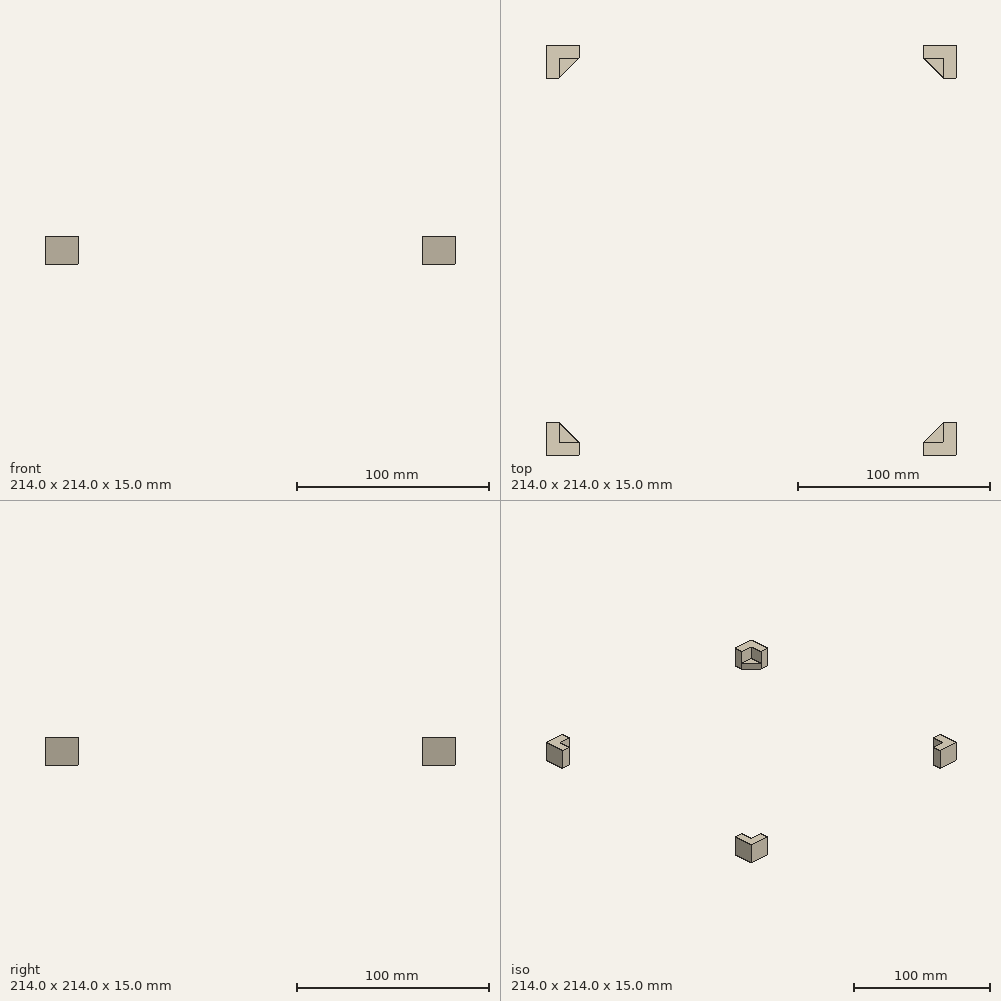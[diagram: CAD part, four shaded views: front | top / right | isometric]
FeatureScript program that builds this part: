
annotation { "Feature Type Name" : "Feature", "Feature Type Description" : "" }
export const myFeature = defineFeature(function(context is Context, id is Id, definition is map)
    precondition{}
    {
        {
            var Q0;
            Q0=qCreatedBy(makeId("Top.planeOp"),FACE);
            var sketch = newSketch(context, id + "F0", { "sketchPlane" : qUnion([Q0])});
            skLineSegment(sketch, "E0.bottom", {"start": v(-107, 107) * mm, "end": v(107, 107) * mm});
            skLineSegment(sketch, "E0.top", {"start": v(-107, -107) * mm, "end": v(107, -107) * mm});
            skLineSegment(sketch, "E0.left", {"start": v(-107, 107) * mm, "end": v(-107, -107) * mm});
            skLineSegment(sketch, "E0.right", {"start": v(107, 107) * mm, "end": v(107, -107) * mm});
            skPoint(sketch, "E0.middle", {"position": v(0, 0) * mm});
            skLineSegment(sketch, "E1.bottom", {"start": v(100, 100) * mm, "end": v(-100, 100) * mm});
            skLineSegment(sketch, "E1.top", {"start": v(100, -100) * mm, "end": v(-100, -100) * mm});
            skLineSegment(sketch, "E1.left", {"start": v(100, 100) * mm, "end": v(100, -100) * mm});
            skLineSegment(sketch, "E1.right", {"start": v(-100, 100) * mm, "end": v(-100, -100) * mm});
            skLineSegment(sketch, "E2.bottom", {"start": v(107, -90) * mm, "end": v(100, -90) * mm});
            skLineSegment(sketch, "E2.top", {"start": v(107, 90) * mm, "end": v(100, 90) * mm});
            skLineSegment(sketch, "E3.left", {"start": v(90, -107) * mm, "end": v(90, -100) * mm});
            skLineSegment(sketch, "E3.right", {"start": v(-90, -107) * mm, "end": v(-90, -100) * mm});
            skLineSegment(sketch, "E4.trimOffspring", {"start": v(-100, 90) * mm, "end": v(-107, 90) * mm});
            skLineSegment(sketch, "E5.trimOffspring", {"start": v(-90, 100) * mm, "end": v(-90, 107) * mm});
            skPoint(sketch, "E6.orphan", {"position": v(-178.54, 90) * mm});
            skPoint(sketch, "E7.orphan", {"position": v(-178.54, -90) * mm});
            skPoint(sketch, "E3.bottom.end.orphan", {"position": v(-90, -205.53) * mm});
            skPoint(sketch, "E8.orphan", {"position": v(90, -205.53) * mm});
            skPoint(sketch, "E3.top.end.orphan", {"position": v(-90, 205.53) * mm});
            skPoint(sketch, "E2.left.start.orphan", {"position": v(178.54, -90) * mm});
            skPoint(sketch, "E9.orphan", {"position": v(178.54, 90) * mm});
            skPoint(sketch, "E10.orphan", {"position": v(90, 205.53) * mm});
            skLineSegment(sketch, "E11.trimOffspring", {"start": v(-100, -90) * mm, "end": v(-107, -90) * mm});
            skLineSegment(sketch, "E12.trimOffspring", {"start": v(90, 100) * mm, "end": v(90, 107) * mm});
            skLineSegment(sketch, "E13", {"start": v(100, -90) * mm, "end": v(90, -100) * mm});
            skLineSegment(sketch, "E14", {"start": v(90, 100) * mm, "end": v(100, 90) * mm});
            skLineSegment(sketch, "E15", {"start": v(-90, -100) * mm, "end": v(-100, -90) * mm});
            skLineSegment(sketch, "E16", {"start": v(-100, 90) * mm, "end": v(-90, 100) * mm});
            skSolve(sketch);
        }
        {
            var Q0;
            {var subQ5=sQuery(id+"F0.wireOp",EDGE,"E4.trimOffspring");Q0=makeQuery(id+"F0.imprint","IMPRINT",FACE,{"disambiguationData":[TD([[makeQuery(id+"F0.imprint","IMPRINT",EDGE,{"derivedFrom":subQ5}),-1.0]])]});}
            var Q1;
            {var subQ4=sQuery(id+"F0.wireOp",EDGE,"E3.right");Q1=makeQuery(id+"F0.imprint","IMPRINT",FACE,{"disambiguationData":[TD([[makeQuery(id+"F0.imprint","IMPRINT",EDGE,{"derivedFrom":subQ4}),1.0]])]});}
            var Q2;
            {var subQ3=sQuery(id+"F0.wireOp",EDGE,"E2.bottom");Q2=makeQuery(id+"F0.imprint","IMPRINT",FACE,{"disambiguationData":[TD([[makeQuery(id+"F0.imprint","IMPRINT",EDGE,{"derivedFrom":subQ3}),1.0]])]});}
            var Q3;
            {var subQ4=sQuery(id+"F0.wireOp",EDGE,"E2.top");Q3=makeQuery(id+"F0.imprint","IMPRINT",FACE,{"disambiguationData":[TD([[makeQuery(id+"F0.imprint","IMPRINT",EDGE,{"derivedFrom":subQ4}),-1.0]])]});}
            extrude(context, id + "F1", {"entities" : qUnion([Q0, Q1, Q2, Q3]), "depth" : 15 * mm, "offsetDistance" : 25 * mm});
        }
        {
            var Q0;
            {var subQ3=sQuery(id+"F0.wireOp",EDGE,"E16");Q0=makeQuery(id+"F0.imprint","IMPRINT",FACE,{"disambiguationData":[TD([[makeQuery(id+"F0.imprint","IMPRINT",EDGE,{"derivedFrom":subQ3}),1.0]])]});}
            var Q1;
            {var subQ3=sQuery(id+"F0.wireOp",EDGE,"E15");Q1=makeQuery(id+"F0.imprint","IMPRINT",FACE,{"disambiguationData":[TD([[makeQuery(id+"F0.imprint","IMPRINT",EDGE,{"derivedFrom":subQ3}),1.0]])]});}
            var Q2;
            {var subQ3=sQuery(id+"F0.wireOp",EDGE,"E13");Q2=makeQuery(id+"F0.imprint","IMPRINT",FACE,{"disambiguationData":[TD([[makeQuery(id+"F0.imprint","IMPRINT",EDGE,{"derivedFrom":subQ3}),1.0]])]});}
            var Q3;
            {var subQ3=sQuery(id+"F0.wireOp",EDGE,"E14");Q3=makeQuery(id+"F0.imprint","IMPRINT",FACE,{"disambiguationData":[TD([[makeQuery(id+"F0.imprint","IMPRINT",EDGE,{"derivedFrom":subQ3}),1.0]])]});}
            extrude(context, id + "F2", {"entities" : qUnion([Q0, Q1, Q2, Q3]), "depth" : 5 * mm, "offsetDistance" : 25 * mm});
        }
    });
